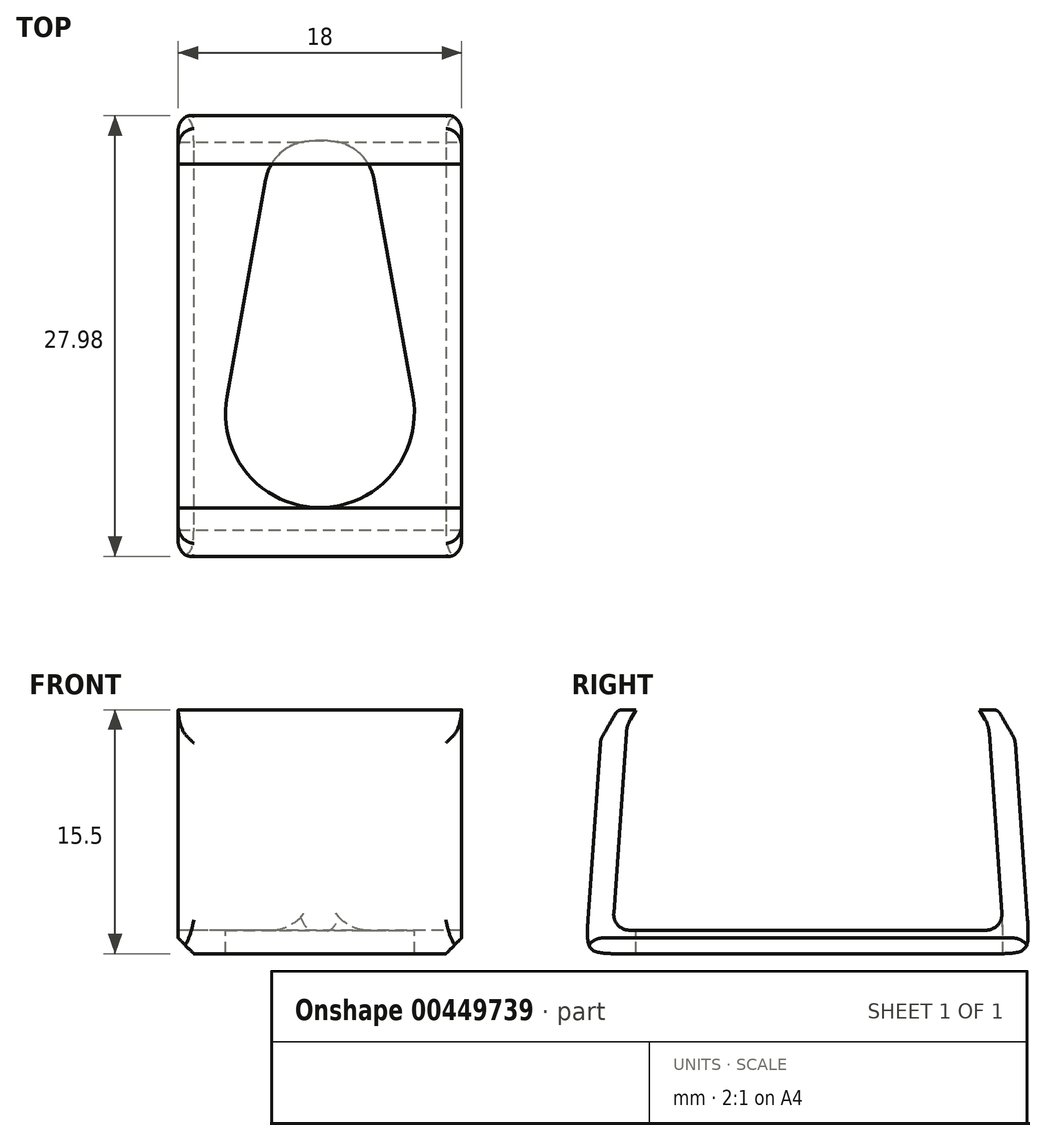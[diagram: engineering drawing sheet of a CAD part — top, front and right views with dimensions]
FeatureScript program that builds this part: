
annotation { "Feature Type Name" : "Feature", "Feature Type Description" : "" }
export const myFeature = defineFeature(function(context is Context, id is Id, definition is map)
    precondition{}
    {
        {
            var Q0;
            Q0=qCreatedBy(makeId("Right.planeOp"),FACE);
            var sketch = newSketch(context, id + "F0", { "sketchPlane" : qUnion([Q0])});
            skLineSegment(sketch, "E0", {"start": v(-14.1, 0) * mm, "end": v(14.1, 0) * mm});
            skLineSegment(sketch, "E1", {"start": v(14.1, 0) * mm, "end": v(13.16, 13.61) * mm});
            skLineSegment(sketch, "E2", {"start": v(13.16, 13.61) * mm, "end": v(12.07, 15.5) * mm});
            skLineSegment(sketch, "E3", {"start": v(12.07, 15.5) * mm, "end": v(10.91, 15.5) * mm});
            skLineSegment(sketch, "E4", {"start": v(10.91, 15.5) * mm, "end": v(11.5, 14.5) * mm});
            skLineSegment(sketch, "E5", {"start": v(11.5, 14.5) * mm, "end": v(12.4, 1.5) * mm});
            skLineSegment(sketch, "E6", {"start": v(12.4, 1.5) * mm, "end": v(-12.4, 1.5) * mm});
            skLineSegment(sketch, "E7", {"start": v(-12.4, 1.5) * mm, "end": v(-11.5, 14.5) * mm});
            skLineSegment(sketch, "E8", {"start": v(-11.5, 14.5) * mm, "end": v(-10.91, 15.5) * mm});
            skLineSegment(sketch, "E9", {"start": v(-10.91, 15.5) * mm, "end": v(-12.07, 15.5) * mm});
            skLineSegment(sketch, "E10", {"start": v(-12.07, 15.5) * mm, "end": v(-13.16, 13.61) * mm});
            skLineSegment(sketch, "E11", {"start": v(-13.16, 13.61) * mm, "end": v(-14.1, 0) * mm});
            skLineSegment(sketch, "E12", {"start": v(-11.5, 14.5) * mm, "end": v(11.5, 14.5) * mm, "construction": true});
            skLineSegment(sketch, "E13", {"start": v(-10.91, 15.5) * mm, "end": v(10.91, 15.5) * mm, "construction": true});
            skSolve(sketch);
        }
        {
            var Q0;
            Q0=makeQuery(id+"F0.imprint","IMPRINT",FACE,{"disambiguationData":[TD([[makeQuery(id+"F0.imprint","IMPRINT",EDGE,{"derivedFrom":sQuery(id+"F0.wireOp",EDGE,"E0")}),1.0]])]});
            extrude(context, id + "F1", {"entities" : qUnion([Q0]), "endBound" : BoundingType.SYMMETRIC, "depth" : 18 * mm});
        }
        {
            var Q0;
            Q0=makeQuery(id+"F1.opExtrude","SWEPT_FACE",FACE,{"disambiguationData":[OSD([sQuery(id+"F0.wireOp",EDGE,"E6")])]});
            var sketch = newSketch(context, id + "F2", { "sketchPlane" : qUnion([Q0])});
            skCircle(sketch, "E14", {"center": v(0, -4.9) * mm, "radius": 6 * mm});
            skLineSegment(sketch, "E15", {"start": v(0, -4.9) * mm, "end": v(0, -10.9) * mm, "construction": true});
            skLineSegment(sketch, "E16", {"start": v(0, -10.9) * mm, "end": v(0, -12.4) * mm, "construction": true});
            skLineSegment(sketch, "E17", {"start": v(-3, 12.4) * mm, "end": v(3, 12.4) * mm});
            skLineSegment(sketch, "E18", {"start": v(-3, 12.4) * mm, "end": v(-5.9, -3.84) * mm});
            skLineSegment(sketch, "E19", {"start": v(3, 12.4) * mm, "end": v(5.9, -3.84) * mm});
            skSolve(sketch);
        }
        {
            var Q0;
            Q0=makeQuery(id+"F2.imprint","IMPRINT",FACE,{"disambiguationData":[TD([[makeQuery(id+"F2.imprint","IMPRINT",EDGE,{"derivedFrom":sQuery(id+"F2.wireOp",EDGE,"E17")}),1.0]])]});
            var Q1;
            {var subQ0=sQuery(id+"F2.wireOp",EDGE,"E14");var subQ1=makeQuery(id+"F2.imprint","INTERSECT",VERTEX,{"derivedFrom":[subQ0,sQuery(id+"F2.wireOp",EDGE,"E18")]});Q1=makeQuery(id+"F2.imprint","IMPRINT",FACE,{"disambiguationData":[TD([[makeQuery(id+"F2.imprint","IMPRINT",EDGE,{"disambiguationData":[TD([[subQ1,1.0]])],"derivedFrom":subQ0}),1.0]])]});}
            extrude(context, id + "F3", {"entities" : qUnion([Q0, Q1]), "operationType" : NewBodyOperationType.REMOVE, "oppositeDirection" : true, "depth" : 25 * mm});
        }
        {
            var Q0;
            Q0=makeQuery(id+"F3.boolean.opBoolean","COPY",EDGE,{"derivedFrom":makeQuery(id+"F3.opExtrude","SWEPT_EDGE",EDGE,{"disambiguationData":[OSD([sQuery(id+"F0.wireOp",EDGE,"E5"),sQuery(id+"F0.wireOp",EDGE,"E6"),sQuery(id+"F2.wireOp",EDGE,"E17"),sQuery(id+"F2.wireOp",EDGE,"E18")])]})});
            var Q1;
            Q1=makeQuery(id+"F3.boolean.opBoolean","COPY",EDGE,{"derivedFrom":makeQuery(id+"F3.opExtrude","SWEPT_EDGE",EDGE,{"disambiguationData":[OSD([sQuery(id+"F0.wireOp",EDGE,"E5"),sQuery(id+"F0.wireOp",EDGE,"E6"),sQuery(id+"F2.wireOp",EDGE,"E17"),sQuery(id+"F2.wireOp",EDGE,"E19")])]})});
            fillet(context, id + "F4", {"entities" : qUnion([Q0, Q1]), "radius" : 3 * mm, "tangentPropagation" : true, "allowEdgeOverflow" : false});
        }
        {
            var Q0;
            Q0=makeQuery(id+"F1.opExtrude","SWEPT_EDGE",EDGE,{"disambiguationData":[OSD([sQuery(id+"F0.wireOp",EDGE,"E6"),sQuery(id+"F0.wireOp",EDGE,"E7")])]});
            var Q1;
            Q1=makeQuery(id+"F1.opExtrude","SWEPT_EDGE",EDGE,{"disambiguationData":[OSD([sQuery(id+"F0.wireOp",EDGE,"E5"),sQuery(id+"F0.wireOp",EDGE,"E6")])]});
            var Q2;
            Q2=makeQuery(id+"F1.opExtrude","SWEPT_EDGE",EDGE,{"disambiguationData":[OSD([sQuery(id+"F0.wireOp",EDGE,"E1"),sQuery(id+"F0.wireOp",EDGE,"E2")])]});
            var Q3;
            Q3=makeQuery(id+"F1.opExtrude","SWEPT_EDGE",EDGE,{"disambiguationData":[OSD([sQuery(id+"F0.wireOp",EDGE,"E10"),sQuery(id+"F0.wireOp",EDGE,"E11")])]});
            fillet(context, id + "F5", {"entities" : qUnion([Q0, Q1, Q2, Q3]), "radius" : 1 * mm, "tangentPropagation" : true, "allowEdgeOverflow" : false});
        }
        {
            var Q0;
            Q0=makeQuery(id+"F1.opExtrude","SWEPT_EDGE",EDGE,{"disambiguationData":[OSD([sQuery(id+"F0.wireOp",EDGE,"E7"),sQuery(id+"F0.wireOp",EDGE,"E8")])]});
            var Q1;
            Q1=makeQuery(id+"F1.opExtrude","SWEPT_EDGE",EDGE,{"disambiguationData":[OSD([sQuery(id+"F0.wireOp",EDGE,"E4"),sQuery(id+"F0.wireOp",EDGE,"E5")])]});
            fillet(context, id + "F6", {"entities" : qUnion([Q0, Q1]), "radius" : 2 * mm, "tangentPropagation" : true, "allowEdgeOverflow" : false});
        }
        {
            var Q0;
            Q0=makeQuery(id+"F1.opExtrude","SWEPT_EDGE",EDGE,{"disambiguationData":[OSD([sQuery(id+"F0.wireOp",EDGE,"E9"),sQuery(id+"F0.wireOp",EDGE,"E10")])]});
            var Q1;
            Q1=makeQuery(id+"F1.opExtrude","SWEPT_EDGE",EDGE,{"disambiguationData":[OSD([sQuery(id+"F0.wireOp",EDGE,"E2"),sQuery(id+"F0.wireOp",EDGE,"E3")])]});
            fillet(context, id + "F7", {"entities" : qUnion([Q0, Q1]), "radius" : .5 * mm, "tangentPropagation" : true, "allowEdgeOverflow" : false});
        }
        {
            var Q0;
            Q0=makeQuery(id+"F1.opExtrude","SWEPT_EDGE",EDGE,{"disambiguationData":[OSD([sQuery(id+"F0.wireOp",EDGE,"E0"),sQuery(id+"F0.wireOp",EDGE,"E11")])]});
            var Q1;
            Q1=makeQuery(id+"F1.opExtrude","SWEPT_EDGE",EDGE,{"disambiguationData":[OSD([sQuery(id+"F0.wireOp",EDGE,"E0"),sQuery(id+"F0.wireOp",EDGE,"E1")])]});
            fillet(context, id + "F8", {"entities" : qUnion([Q0, Q1]), "radius" : 2 * mm, "tangentPropagation" : true, "rho" : .7, "crossSection" : FilletCrossSection.CONIC, "allowEdgeOverflow" : false});
        }
        {
            var Q0;
            Q0=makeQuery(id+"F1.opExtrude","CAP_EDGE",EDGE,{"disambiguationData":[OSD([sQuery(id+"F0.wireOp",EDGE,"E0")])],"isStart":false});
            var Q1;
            Q1=makeQuery(id+"F1.opExtrude","CAP_EDGE",EDGE,{"disambiguationData":[OSD([sQuery(id+"F0.wireOp",EDGE,"E0")])],"isStart":true});
            chamfer(context, id + "F9", {"entities" : qUnion([Q0, Q1]), "width" : 1 * mm});
        }
        {
            var Q0;
            Q0=makeQuery(id+"F1.opExtrude","CAP_EDGE",EDGE,{"disambiguationData":[OSD([sQuery(id+"F0.wireOp",EDGE,"E11")])],"isStart":false});
            var Q1;
            Q1=makeQuery(id+"F1.opExtrude","CAP_EDGE",EDGE,{"disambiguationData":[OSD([sQuery(id+"F0.wireOp",EDGE,"E1")])],"isStart":false});
            var Q2;
            Q2=makeQuery(id+"F1.opExtrude","CAP_EDGE",EDGE,{"disambiguationData":[OSD([sQuery(id+"F0.wireOp",EDGE,"E11")])],"isStart":true});
            var Q3;
            Q3=makeQuery(id+"F1.opExtrude","CAP_EDGE",EDGE,{"disambiguationData":[OSD([sQuery(id+"F0.wireOp",EDGE,"E1")])],"isStart":true});
            fillet(context, id + "F10", {"entities" : qUnion([Q0, Q1, Q2, Q3]), "radius" : 1 * mm, "allowEdgeOverflow" : false});
        }
    });
